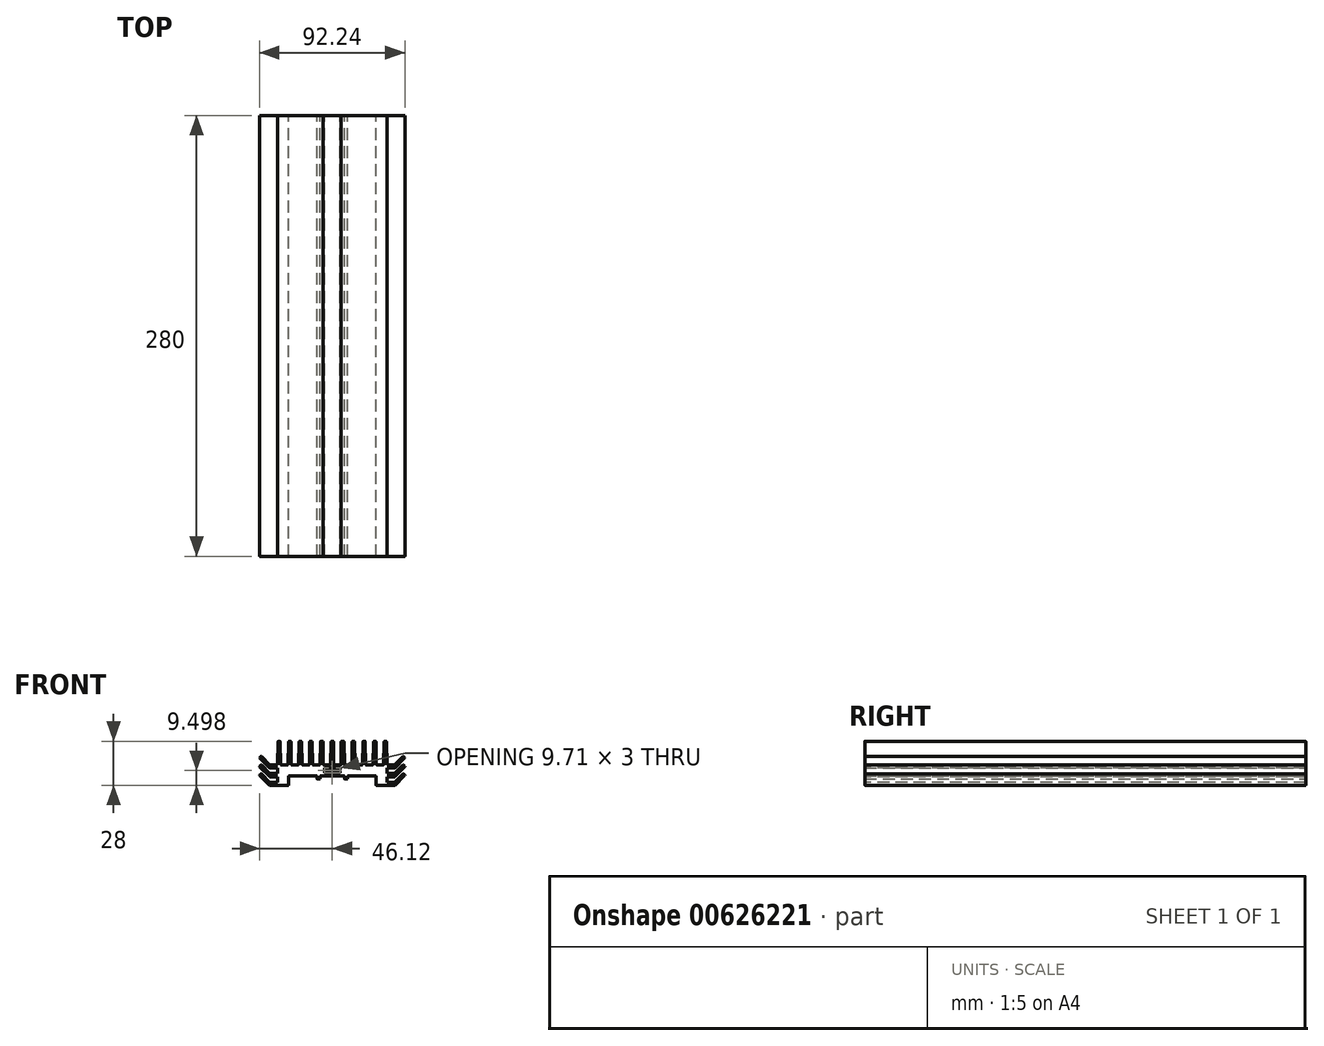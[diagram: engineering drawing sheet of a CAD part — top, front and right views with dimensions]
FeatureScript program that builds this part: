
annotation { "Feature Type Name" : "Feature", "Feature Type Description" : "" }
export const myFeature = defineFeature(function(context is Context, id is Id, definition is map)
    precondition{}
    {
        {
            var Q0;
            Q0=qCreatedBy(makeId("Front.planeOp"),FACE);
            var sketch = newSketch(context, id + "F0", { "sketchPlane" : qUnion([Q0])});
            skLineSegment(sketch, "E0", {"start": v(-9.75, -3.7) * mm, "end": v(-9.75, -5.3) * mm});
            skLineSegment(sketch, "E1", {"start": v(-9.55, -5.5) * mm, "end": v(-7.95, -5.5) * mm});
            skLineSegment(sketch, "E2.1.0.0", {"start": v(-33, 18.3) * mm, "end": v(-32.75, 3.7) * mm});
            skLineSegment(sketch, "E2.1.0.1", {"start": v(-32.55, 3.5) * mm, "end": v(-28.2, 3.5) * mm});
            skLineSegment(sketch, "E2.1.0.2", {"start": v(-34.75, 3.7) * mm, "end": v(-34.5, 18.3) * mm});
            skLineSegment(sketch, "E2.1.0.3", {"start": v(-34.3, 18.5) * mm, "end": v(-33.2, 18.5) * mm});
            skLineSegment(sketch, "E2.2.0.0", {"start": v(-26.25, 18.3) * mm, "end": v(-26, 3.7) * mm});
            skLineSegment(sketch, "E2.2.0.1", {"start": v(-25.8, 3.5) * mm, "end": v(-21.45, 3.5) * mm});
            skLineSegment(sketch, "E2.2.0.2", {"start": v(-28, 3.7) * mm, "end": v(-27.75, 18.3) * mm});
            skLineSegment(sketch, "E2.2.0.3", {"start": v(-27.55, 18.5) * mm, "end": v(-26.45, 18.5) * mm});
            skLineSegment(sketch, "E2.3.0.0", {"start": v(-19.5, 18.3) * mm, "end": v(-19.25, 3.7) * mm});
            skLineSegment(sketch, "E2.3.0.1", {"start": v(-19.05, 3.5) * mm, "end": v(-14.7, 3.5) * mm});
            skLineSegment(sketch, "E2.3.0.2", {"start": v(-21.25, 3.7) * mm, "end": v(-21, 18.3) * mm});
            skLineSegment(sketch, "E2.3.0.3", {"start": v(-20.8, 18.5) * mm, "end": v(-19.7, 18.5) * mm});
            skLineSegment(sketch, "E2.4.0.0", {"start": v(-12.75, 18.3) * mm, "end": v(-12.5, 3.7) * mm});
            skLineSegment(sketch, "E2.4.0.1", {"start": v(-12.3, 3.5) * mm, "end": v(-7.95, 3.5) * mm});
            skLineSegment(sketch, "E2.4.0.2", {"start": v(-14.5, 3.7) * mm, "end": v(-14.25, 18.3) * mm});
            skLineSegment(sketch, "E2.4.0.3", {"start": v(-14.05, 18.5) * mm, "end": v(-12.95, 18.5) * mm});
            skLineSegment(sketch, "E2.5.0.0", {"start": v(-5.75, 18.3) * mm, "end": v(-5.75, 3.7) * mm});
            skLineSegment(sketch, "E2.5.0.1", {"start": v(-5.55, 3.5) * mm, "end": v(-1.2, 3.5) * mm});
            skLineSegment(sketch, "E2.5.0.2", {"start": v(-7.75, 3.7) * mm, "end": v(-7.5, 18.3) * mm});
            skLineSegment(sketch, "E2.5.0.3", {"start": v(-7.3, 18.5) * mm, "end": v(-5.95, 18.5) * mm});
            skLineSegment(sketch, "E3.6.6.0", {"start": v(-1, 3.7) * mm, "end": v(-0.75, 18.3) * mm});
            skLineSegment(sketch, "E3.9.6.0", {"start": v(-0.55, 18.5) * mm, "end": v(0, 18.5) * mm});
            skPoint(sketch, "E4", {"position": v(0, 18.5) * mm});
            skLineSegment(sketch, "E5", {"start": v(0, 18.5) * mm, "end": v(0, 1.5) * mm});
            skLineSegment(sketch, "E6", {"start": v(-4.85, 1.3) * mm, "end": v(-4.85, -1.3) * mm});
            skLineSegment(sketch, "E7", {"start": v(0, -1.5) * mm, "end": v(0, -3.5) * mm});
            skLineSegment(sketch, "E8", {"start": v(-7.75, -3.7) * mm, "end": v(-7.75, -5.3) * mm});
            skPoint(sketch, "E9.visualSharp", {"position": v(-34.5, 18.5) * mm});
            skArc(sketch, "E9.filletArc", {"start": v(-34.3, 18.5) * mm, "mid": v(-34.44, 18.44) * mm, "end": v(-34.5, 18.3) * mm});
            skPoint(sketch, "E10.visualSharp", {"position": v(-33, 18.5) * mm});
            skArc(sketch, "E10.filletArc", {"start": v(-33, 18.3) * mm, "mid": v(-33.06, 18.44) * mm, "end": v(-33.2, 18.5) * mm});
            skPoint(sketch, "E11.visualSharp", {"position": v(-27.75, 18.5) * mm});
            skArc(sketch, "E11.filletArc", {"start": v(-27.55, 18.5) * mm, "mid": v(-27.7, 18.44) * mm, "end": v(-27.75, 18.3) * mm});
            skPoint(sketch, "E12.visualSharp", {"position": v(-26.25, 18.5) * mm});
            skArc(sketch, "E12.filletArc", {"start": v(-26.25, 18.3) * mm, "mid": v(-26.3, 18.44) * mm, "end": v(-26.45, 18.5) * mm});
            skPoint(sketch, "E13.visualSharp", {"position": v(-21, 18.5) * mm});
            skArc(sketch, "E13.filletArc", {"start": v(-20.8, 18.5) * mm, "mid": v(-20.94, 18.44) * mm, "end": v(-21, 18.3) * mm});
            skPoint(sketch, "E14.visualSharp", {"position": v(-19.5, 18.5) * mm});
            skArc(sketch, "E14.filletArc", {"start": v(-19.5, 18.3) * mm, "mid": v(-19.56, 18.44) * mm, "end": v(-19.7, 18.5) * mm});
            skPoint(sketch, "E15.visualSharp", {"position": v(-14.25, 18.5) * mm});
            skArc(sketch, "E15.filletArc", {"start": v(-14.05, 18.5) * mm, "mid": v(-14.2, 18.44) * mm, "end": v(-14.25, 18.3) * mm});
            skPoint(sketch, "E16.visualSharp", {"position": v(-12.75, 18.5) * mm});
            skArc(sketch, "E16.filletArc", {"start": v(-12.75, 18.3) * mm, "mid": v(-12.8, 18.44) * mm, "end": v(-12.95, 18.5) * mm});
            skPoint(sketch, "E17.visualSharp", {"position": v(-7.5, 18.5) * mm});
            skArc(sketch, "E17.filletArc", {"start": v(-7.3, 18.5) * mm, "mid": v(-7.44, 18.44) * mm, "end": v(-7.5, 18.3) * mm});
            skPoint(sketch, "E18.visualSharp", {"position": v(-5.75, 18.5) * mm});
            skArc(sketch, "E18.filletArc", {"start": v(-5.75, 18.3) * mm, "mid": v(-5.8, 18.44) * mm, "end": v(-5.95, 18.5) * mm});
            skPoint(sketch, "E19.visualSharp", {"position": v(-0.75, 18.5) * mm});
            skArc(sketch, "E19.filletArc", {"start": v(-0.55, 18.5) * mm, "mid": v(-0.7, 18.44) * mm, "end": v(-0.75, 18.3) * mm});
            skPoint(sketch, "E20.visualSharp", {"position": v(0, 1.5) * mm});
            skPoint(sketch, "E21.visualSharp", {"position": v(-4.85, 1.5) * mm});
            skArc(sketch, "E21.filletArc", {"start": v(-4.65, 1.5) * mm, "mid": v(-4.8, 1.44) * mm, "end": v(-4.85, 1.3) * mm});
            skPoint(sketch, "E22.visualSharp", {"position": v(-4.85, -1.5) * mm});
            skArc(sketch, "E22.filletArc", {"start": v(-4.85, -1.3) * mm, "mid": v(-4.8, -1.44) * mm, "end": v(-4.65, -1.5) * mm});
            skPoint(sketch, "E23.visualSharp", {"position": v(0, -1.5) * mm});
            skPoint(sketch, "E24.visualSharp", {"position": v(0, -3.5) * mm});
            skPoint(sketch, "E25.visualSharp", {"position": v(-7.75, -3.5) * mm});
            skArc(sketch, "E25.filletArc", {"start": v(-7.55, -3.5) * mm, "mid": v(-7.7, -3.56) * mm, "end": v(-7.75, -3.7) * mm});
            skPoint(sketch, "E26.visualSharp", {"position": v(-7.75, -5.5) * mm});
            skArc(sketch, "E26.filletArc", {"start": v(-7.95, -5.5) * mm, "mid": v(-7.8, -5.44) * mm, "end": v(-7.75, -5.3) * mm});
            skPoint(sketch, "E27.visualSharp", {"position": v(-9.75, -5.5) * mm});
            skArc(sketch, "E27.filletArc", {"start": v(-9.75, -5.3) * mm, "mid": v(-9.7, -5.44) * mm, "end": v(-9.55, -5.5) * mm});
            skPoint(sketch, "E28.visualSharp", {"position": v(-9.75, -3.5) * mm});
            skArc(sketch, "E28.filletArc", {"start": v(-9.75, -3.7) * mm, "mid": v(-9.8, -3.56) * mm, "end": v(-9.95, -3.5) * mm});
            skPoint(sketch, "E29.visualSharp", {"position": v(-32.75, 3.5) * mm});
            skArc(sketch, "E29.filletArc", {"start": v(-32.75, 3.7) * mm, "mid": v(-32.7, 3.56) * mm, "end": v(-32.55, 3.5) * mm});
            skPoint(sketch, "E30.visualSharp", {"position": v(-28, 3.5) * mm});
            skArc(sketch, "E30.filletArc", {"start": v(-28.2, 3.5) * mm, "mid": v(-28.06, 3.56) * mm, "end": v(-28, 3.7) * mm});
            skPoint(sketch, "E31.visualSharp", {"position": v(-26, 3.5) * mm});
            skArc(sketch, "E31.filletArc", {"start": v(-26, 3.7) * mm, "mid": v(-25.94, 3.56) * mm, "end": v(-25.8, 3.5) * mm});
            skPoint(sketch, "E32.visualSharp", {"position": v(-21.25, 3.5) * mm});
            skArc(sketch, "E32.filletArc", {"start": v(-21.45, 3.5) * mm, "mid": v(-21.3, 3.56) * mm, "end": v(-21.25, 3.7) * mm});
            skPoint(sketch, "E33.visualSharp", {"position": v(-19.25, 3.5) * mm});
            skArc(sketch, "E33.filletArc", {"start": v(-19.25, 3.7) * mm, "mid": v(-19.2, 3.56) * mm, "end": v(-19.05, 3.5) * mm});
            skPoint(sketch, "E34.visualSharp", {"position": v(-14.5, 3.5) * mm});
            skArc(sketch, "E34.filletArc", {"start": v(-14.7, 3.5) * mm, "mid": v(-14.56, 3.56) * mm, "end": v(-14.5, 3.7) * mm});
            skPoint(sketch, "E35.visualSharp", {"position": v(-12.5, 3.5) * mm});
            skArc(sketch, "E35.filletArc", {"start": v(-12.5, 3.7) * mm, "mid": v(-12.44, 3.56) * mm, "end": v(-12.3, 3.5) * mm});
            skPoint(sketch, "E36.visualSharp", {"position": v(-7.75, 3.5) * mm});
            skArc(sketch, "E36.filletArc", {"start": v(-7.95, 3.5) * mm, "mid": v(-7.8, 3.56) * mm, "end": v(-7.75, 3.7) * mm});
            skPoint(sketch, "E37.visualSharp", {"position": v(-5.75, 3.5) * mm});
            skArc(sketch, "E37.filletArc", {"start": v(-5.75, 3.7) * mm, "mid": v(-5.7, 3.56) * mm, "end": v(-5.55, 3.5) * mm});
            skPoint(sketch, "E38.visualSharp", {"position": v(-1, 3.5) * mm});
            skArc(sketch, "E38.filletArc", {"start": v(-1.2, 3.5) * mm, "mid": v(-1.06, 3.56) * mm, "end": v(-1, 3.7) * mm});
            skLineSegment(sketch, "E39", {"start": v(-4.65, 1.5) * mm, "end": v(0, 1.5) * mm});
            skLineSegment(sketch, "E40", {"start": v(-4.65, -1.5) * mm, "end": v(0, -1.5) * mm});
            skLineSegment(sketch, "E41", {"start": v(-7.55, -3.5) * mm, "end": v(0, -3.5) * mm});
            skLineSegment(sketch, "E42", {"start": v(-9.95, -3.5) * mm, "end": v(-27.55, -3.5) * mm});
            skLineSegment(sketch, "E43", {"start": v(-27.75, -3.7) * mm, "end": v(-27.75, -9.3) * mm});
            skPoint(sketch, "E44.visualSharp", {"position": v(-27.75, -9.5) * mm});
            skArc(sketch, "E44.filletArc", {"start": v(-27.95, -9.5) * mm, "mid": v(-27.8, -9.44) * mm, "end": v(-27.75, -9.3) * mm});
            skPoint(sketch, "E45.visualSharp", {"position": v(-27.75, -3.5) * mm});
            skArc(sketch, "E45.filletArc", {"start": v(-27.55, -3.5) * mm, "mid": v(-27.69, -3.56) * mm, "end": v(-27.75, -3.7) * mm});
            skLineSegment(sketch, "E46", {"start": v(-34.75, 3.7) * mm, "end": v(-34.75, -9.5) * mm});
            skLineSegment(sketch, "E47", {"start": v(-27.95, -9.5) * mm, "end": v(-34.75, -9.5) * mm});
            skSolve(sketch);
        }
        {
            var Q0;
            Q0=qSketchRegion(id+"F0",true);
            extrude(context, id + "F1", {"entities" : qUnion([Q0]), "depth" : 280 * mm, "offsetDistance" : 25 * mm});
        }
        {
            var Q0;
            Q0=makeQuery(id+"F1.opExtrude","CAP_FACE",FACE,{"disambiguationData":[OSD([sQuery(id+"F0.wireOp",EDGE,"E0"),sQuery(id+"F0.wireOp",EDGE,"E1"),sQuery(id+"F0.wireOp",EDGE,"E2.1.0.0"),sQuery(id+"F0.wireOp",EDGE,"E2.1.0.1"),sQuery(id+"F0.wireOp",EDGE,"E2.1.0.2"),sQuery(id+"F0.wireOp",EDGE,"E2.1.0.3"),sQuery(id+"F0.wireOp",EDGE,"E2.2.0.0"),sQuery(id+"F0.wireOp",EDGE,"E2.2.0.1"),sQuery(id+"F0.wireOp",EDGE,"E2.2.0.2"),sQuery(id+"F0.wireOp",EDGE,"E2.2.0.3"),sQuery(id+"F0.wireOp",EDGE,"E2.3.0.0"),sQuery(id+"F0.wireOp",EDGE,"E2.3.0.1"),sQuery(id+"F0.wireOp",EDGE,"E2.3.0.2"),sQuery(id+"F0.wireOp",EDGE,"E2.3.0.3"),sQuery(id+"F0.wireOp",EDGE,"E2.4.0.0"),sQuery(id+"F0.wireOp",EDGE,"E2.4.0.1"),sQuery(id+"F0.wireOp",EDGE,"E2.4.0.2"),sQuery(id+"F0.wireOp",EDGE,"E2.4.0.3"),sQuery(id+"F0.wireOp",EDGE,"E2.5.0.0"),sQuery(id+"F0.wireOp",EDGE,"E2.5.0.1"),sQuery(id+"F0.wireOp",EDGE,"E2.5.0.2"),sQuery(id+"F0.wireOp",EDGE,"E2.5.0.3"),sQuery(id+"F0.wireOp",EDGE,"E3.6.6.0"),sQuery(id+"F0.wireOp",EDGE,"E3.9.6.0"),sQuery(id+"F0.wireOp",EDGE,"E5"),sQuery(id+"F0.wireOp",EDGE,"E6"),sQuery(id+"F0.wireOp",EDGE,"E7"),sQuery(id+"F0.wireOp",EDGE,"E8"),sQuery(id+"F0.wireOp",EDGE,"E9.filletArc"),sQuery(id+"F0.wireOp",EDGE,"E10.filletArc"),sQuery(id+"F0.wireOp",EDGE,"E11.filletArc"),sQuery(id+"F0.wireOp",EDGE,"E12.filletArc"),sQuery(id+"F0.wireOp",EDGE,"E13.filletArc"),sQuery(id+"F0.wireOp",EDGE,"E14.filletArc"),sQuery(id+"F0.wireOp",EDGE,"E15.filletArc"),sQuery(id+"F0.wireOp",EDGE,"E16.filletArc"),sQuery(id+"F0.wireOp",EDGE,"E17.filletArc"),sQuery(id+"F0.wireOp",EDGE,"E18.filletArc"),sQuery(id+"F0.wireOp",EDGE,"E19.filletArc"),sQuery(id+"F0.wireOp",EDGE,"E21.filletArc"),sQuery(id+"F0.wireOp",EDGE,"E22.filletArc"),sQuery(id+"F0.wireOp",EDGE,"E25.filletArc"),sQuery(id+"F0.wireOp",EDGE,"E26.filletArc"),sQuery(id+"F0.wireOp",EDGE,"E27.filletArc"),sQuery(id+"F0.wireOp",EDGE,"E28.filletArc"),sQuery(id+"F0.wireOp",EDGE,"E29.filletArc"),sQuery(id+"F0.wireOp",EDGE,"E30.filletArc"),sQuery(id+"F0.wireOp",EDGE,"E31.filletArc"),sQuery(id+"F0.wireOp",EDGE,"E32.filletArc"),sQuery(id+"F0.wireOp",EDGE,"E33.filletArc"),sQuery(id+"F0.wireOp",EDGE,"E34.filletArc"),sQuery(id+"F0.wireOp",EDGE,"E35.filletArc"),sQuery(id+"F0.wireOp",EDGE,"E36.filletArc"),sQuery(id+"F0.wireOp",EDGE,"E37.filletArc"),sQuery(id+"F0.wireOp",EDGE,"E38.filletArc"),sQuery(id+"F0.wireOp",EDGE,"E39"),sQuery(id+"F0.wireOp",EDGE,"E40"),sQuery(id+"F0.wireOp",EDGE,"E41"),sQuery(id+"F0.wireOp",EDGE,"UyrvhKvo-Hriy-DGAL-Pid4-MuuIVOQ2I04g"),sQuery(id+"F0.wireOp",EDGE,"U6ICKPt3-iNcd-rmJ2-pTeO-fHKRQgZmkzro"),sQuery(id+"F0.wireOp",EDGE,"E42"),sQuery(id+"F0.wireOp",EDGE,"E43"),sQuery(id+"F0.wireOp",EDGE,"E44.filletArc"),sQuery(id+"F0.wireOp",EDGE,"1ba531c4-4689-4158-b5fc-088271326b5e.filletArc"),sQuery(id+"F0.wireOp",EDGE,"E45.filletArc")])],"isStart":false});
            var sketch = newSketch(context, id + "F2", { "sketchPlane" : qUnion([Q0])});
            skLineSegment(sketch, "E48", {"start": v(-34.75, -7.5) * mm, "end": v(-39.54, -7.5) * mm});
            skLineSegment(sketch, "E49", {"start": v(-34.75, -9.5) * mm, "end": v(-39.75, -9.5) * mm});
            skLineSegment(sketch, "E50", {"start": v(-39.68, -7.45) * mm, "end": v(-45, -2.13) * mm});
            skLineSegment(sketch, "E51", {"start": v(-39.8, -9.44) * mm, "end": v(-46.06, -3.19) * mm});
            skLineSegment(sketch, "E52", {"start": v(-45.28, -2.13) * mm, "end": v(-46.06, -2.9) * mm});
            skLineSegment(sketch, "E53", {"start": v(-34.75, -7.5) * mm, "end": v(-34.75, -9.5) * mm});
            skLineSegment(sketch, "E54.direction2", {"start": v(-39.75, -9.5) * mm, "end": v(-39.75, -4) * mm, "construction": true});
            skPoint(sketch, "E55.visualSharp", {"position": v(-39.62, -7.5) * mm});
            skArc(sketch, "E55.filletArc", {"start": v(-39.68, -7.45) * mm, "mid": v(-39.62, -7.49) * mm, "end": v(-39.54, -7.5) * mm});
            skPoint(sketch, "E56.visualSharp", {"position": v(-45.14, -1.99) * mm});
            skArc(sketch, "E56.filletArc", {"start": v(-45, -2.13) * mm, "mid": v(-45.14, -2.07) * mm, "end": v(-45.28, -2.13) * mm});
            skPoint(sketch, "E57.visualSharp", {"position": v(-46.2, -3.05) * mm});
            skArc(sketch, "E57.filletArc", {"start": v(-46.06, -2.9) * mm, "mid": v(-46.12, -3.05) * mm, "end": v(-46.06, -3.19) * mm});
            skPoint(sketch, "E58.visualSharp", {"position": v(-39.75, -9.5) * mm});
            skArc(sketch, "E58.filletArc", {"start": v(-39.8, -9.44) * mm, "mid": v(-39.74, -9.48) * mm, "end": v(-39.66, -9.5) * mm});
            skLineSegment(sketch, "E59.0.1.0", {"start": v(-34.75, -2) * mm, "end": v(-34.75, -4) * mm});
            skLineSegment(sketch, "E59.0.1.1", {"start": v(-39.75, -4) * mm, "end": v(-39.75, 1.5) * mm, "construction": true});
            skPoint(sketch, "E59.0.1.2", {"position": v(-46.2, 2.45) * mm});
            skLineSegment(sketch, "E59.0.1.3", {"start": v(-39.8, -3.94) * mm, "end": v(-46.06, 2.31) * mm});
            skLineSegment(sketch, "E59.0.1.4", {"start": v(-34.75, -2) * mm, "end": v(-39.54, -2) * mm});
            skLineSegment(sketch, "E59.0.1.5", {"start": v(-34.75, -4) * mm, "end": v(-39.75, -4) * mm});
            skPoint(sketch, "E59.0.1.6", {"position": v(-45.14, 3.51) * mm});
            skPoint(sketch, "E59.0.1.7", {"position": v(-39.62, -2) * mm});
            skLineSegment(sketch, "E59.0.1.8", {"start": v(-39.68, -1.95) * mm, "end": v(-45, 3.37) * mm});
            skPoint(sketch, "E59.0.1.9", {"position": v(-39.75, -4) * mm});
            skLineSegment(sketch, "E59.0.1.10", {"start": v(-45.28, 3.37) * mm, "end": v(-46.06, 2.6) * mm});
            skArc(sketch, "E59.0.1.11", {"start": v(-46.06, 2.6) * mm, "mid": v(-46.12, 2.45) * mm, "end": v(-46.06, 2.31) * mm});
            skArc(sketch, "E59.0.1.12", {"start": v(-45, 3.37) * mm, "mid": v(-45.14, 3.43) * mm, "end": v(-45.28, 3.37) * mm});
            skArc(sketch, "E59.0.1.13", {"start": v(-39.68, -1.95) * mm, "mid": v(-39.62, -1.99) * mm, "end": v(-39.54, -2) * mm});
            skArc(sketch, "E59.0.1.14", {"start": v(-39.8, -3.94) * mm, "mid": v(-39.74, -3.98) * mm, "end": v(-39.66, -4) * mm});
            skLineSegment(sketch, "E59.0.2.0", {"start": v(-34.75, 3.5) * mm, "end": v(-34.75, 1.5) * mm});
            skLineSegment(sketch, "E59.0.2.1", {"start": v(-39.75, 1.5) * mm, "end": v(-39.75, 7) * mm, "construction": true});
            skPoint(sketch, "E59.0.2.2", {"position": v(-46.2, 7.95) * mm});
            skLineSegment(sketch, "E59.0.2.3", {"start": v(-39.8, 1.56) * mm, "end": v(-46.06, 7.81) * mm});
            skLineSegment(sketch, "E59.0.2.4", {"start": v(-34.75, 3.5) * mm, "end": v(-39.54, 3.5) * mm});
            skLineSegment(sketch, "E59.0.2.5", {"start": v(-34.75, 1.5) * mm, "end": v(-39.75, 1.5) * mm});
            skPoint(sketch, "E59.0.2.6", {"position": v(-45.14, 9.01) * mm});
            skPoint(sketch, "E59.0.2.7", {"position": v(-39.62, 3.5) * mm});
            skLineSegment(sketch, "E59.0.2.8", {"start": v(-39.68, 3.55) * mm, "end": v(-45, 8.87) * mm});
            skPoint(sketch, "E59.0.2.9", {"position": v(-39.75, 1.5) * mm});
            skLineSegment(sketch, "E59.0.2.10", {"start": v(-45.28, 8.87) * mm, "end": v(-46.06, 8.1) * mm});
            skArc(sketch, "E59.0.2.11", {"start": v(-46.06, 8.1) * mm, "mid": v(-46.12, 7.95) * mm, "end": v(-46.06, 7.81) * mm});
            skArc(sketch, "E59.0.2.12", {"start": v(-45, 8.87) * mm, "mid": v(-45.14, 8.93) * mm, "end": v(-45.28, 8.87) * mm});
            skArc(sketch, "E59.0.2.13", {"start": v(-39.68, 3.55) * mm, "mid": v(-39.62, 3.51) * mm, "end": v(-39.54, 3.5) * mm});
            skArc(sketch, "E59.0.2.14", {"start": v(-39.8, 1.56) * mm, "mid": v(-39.74, 1.52) * mm, "end": v(-39.66, 1.5) * mm});
            skLineSegment(sketch, "E59.direction1", {"start": v(-39.75, -9.5) * mm, "end": v(-14.75, -9.5) * mm, "construction": true});
            skSolve(sketch);
        }
        {
            var Q0;
            Q0=qSketchRegion(id+"F2",true);
            extrude(context, id + "F3", {"entities" : qUnion([Q0]), "operationType" : NewBodyOperationType.ADD, "oppositeDirection" : true, "depth" : 280 * mm, "offsetDistance" : 25 * mm});
        }
        {
            var Q0;
            Q0=makeQuery(id+"F1.opExtrude","SWEPT_BODY",BODY,{"disambiguationData":[OSD([sQuery(id+"F0.wireOp",EDGE,"QOM90pkH-KK3E-2t4G-PR0d-VXwYNY4fjtTb"),sQuery(id+"F0.wireOp",EDGE,"Wt8m1K6G-Pg8W-yz88-BKp3-o8GU5yjb4NPO"),sQuery(id+"F0.wireOp",EDGE,"F3vcOgBq-LlWr-xvjw-e04Y-niSAJOFfG4p2"),sQuery(id+"F0.wireOp",EDGE,"u1mY0JJN-f7Kk-nBfH-W6HL-n9qIg2MDpbPP"),sQuery(id+"F0.wireOp",EDGE,"QIDlm4V3-j7gJ-oFi3-cvUC-kSezUPiWFmIS"),sQuery(id+"F0.wireOp",EDGE,"6xrvO9A8-pm1h-AeFb-QTYX-2HOc3FF3rfEQ"),sQuery(id+"F0.wireOp",EDGE,"Nf9yDHwn-gt6s-M4IA-LLNt-3061gzFxuUBp"),sQuery(id+"F0.wireOp",EDGE,"WuwbFeWC-LNyf-1R1Z-RHmS-f9KyMF8TMt9i"),sQuery(id+"F0.wireOp",EDGE,"UM4JaTJU-Vk1M-XgEN-ImDx-eCgJd49Y6FMu"),sQuery(id+"F0.wireOp",EDGE,"OvlMNyBG-IFKC-w7DX-ZWVS-3YzXS4CVPNQT"),sQuery(id+"F0.wireOp",EDGE,"jmIuwl2N-ih4h-DjTB-hYCO-kHODNnBOpXJs"),sQuery(id+"F0.wireOp",EDGE,"bhDqv4Mq-hX6j-4xH4-fuLw-w89xF4HoMTrF"),sQuery(id+"F0.wireOp",EDGE,"E0"),sQuery(id+"F0.wireOp",EDGE,"E1"),sQuery(id+"F0.wireOp",EDGE,"DATJw4Rr-6OHI-e9sL-mig8-pdpoUj6XXJZJ"),sQuery(id+"F0.wireOp",EDGE,"ed90f767-a289-48e3-8617-8c3c22fb4d72.trimOffspring"),sQuery(id+"F0.wireOp",EDGE,"7ho3JKrC-G9q0-DxLB-qz2V-eUSqsKLsZmBJ"),sQuery(id+"F0.wireOp",EDGE,"Nb5lTvUm-lXxh-YIyg-5x1b-LZ3tmgTk2abY"),sQuery(id+"F0.wireOp",EDGE,"Z2SCv61l-lqp3-au7K-zo4L-WJUViGbaLhYw"),sQuery(id+"F0.wireOp",EDGE,"qlelKb4N-GS20-CHXp-tJnn-sWviO8Gk2iGX"),sQuery(id+"F0.wireOp",EDGE,"E2.1.0.0"),sQuery(id+"F0.wireOp",EDGE,"E2.1.0.1"),sQuery(id+"F0.wireOp",EDGE,"E2.1.0.2"),sQuery(id+"F0.wireOp",EDGE,"E2.1.0.3"),sQuery(id+"F0.wireOp",EDGE,"E2.2.0.0"),sQuery(id+"F0.wireOp",EDGE,"E2.2.0.1"),sQuery(id+"F0.wireOp",EDGE,"E2.2.0.2"),sQuery(id+"F0.wireOp",EDGE,"E2.2.0.3"),sQuery(id+"F0.wireOp",EDGE,"E2.3.0.0"),sQuery(id+"F0.wireOp",EDGE,"E2.3.0.1"),sQuery(id+"F0.wireOp",EDGE,"E2.3.0.2"),sQuery(id+"F0.wireOp",EDGE,"E2.3.0.3"),sQuery(id+"F0.wireOp",EDGE,"E2.4.0.0"),sQuery(id+"F0.wireOp",EDGE,"E2.4.0.1"),sQuery(id+"F0.wireOp",EDGE,"E2.4.0.2"),sQuery(id+"F0.wireOp",EDGE,"E2.4.0.3"),sQuery(id+"F0.wireOp",EDGE,"E2.5.0.0"),sQuery(id+"F0.wireOp",EDGE,"E2.5.0.1"),sQuery(id+"F0.wireOp",EDGE,"E2.5.0.2"),sQuery(id+"F0.wireOp",EDGE,"E2.5.0.3"),sQuery(id+"F0.wireOp",EDGE,"E3.6.6.0"),sQuery(id+"F0.wireOp",EDGE,"E3.9.6.0"),sQuery(id+"F0.wireOp",EDGE,"yGFb3Jfo-Lhlh-xzfz-Ljs9-34xcXF1H7Gp1"),sQuery(id+"F0.wireOp",EDGE,"dxc8wIRG-n3ac-7oqY-UQSt-FR4flQWY79jH"),sQuery(id+"F0.wireOp",EDGE,"pMfyub31-Xo22-kmQh-hgcO-EaUa3d53Z9ym"),sQuery(id+"F0.wireOp",EDGE,"EXS0VTzR-uZRH-gpkk-ciJv-APifiNII5ex7"),sQuery(id+"F0.wireOp",EDGE,"j9COY3aO-4lFf-zBAU-mgS4-eOpnypJtWWPn")])]});
            var Q1;
            Q1=makeQuery(id+"F1.opExtrude","SWEPT_FACE",FACE,{"disambiguationData":[OSD([sQuery(id+"F0.wireOp",EDGE,"E5")])]});
            mirror(context, id + "F4", {"operationType" : NewBodyOperationType.ADD, "entities" : qUnion([Q0]), "mirrorPlane" : qUnion([Q1])});
        }
    });
